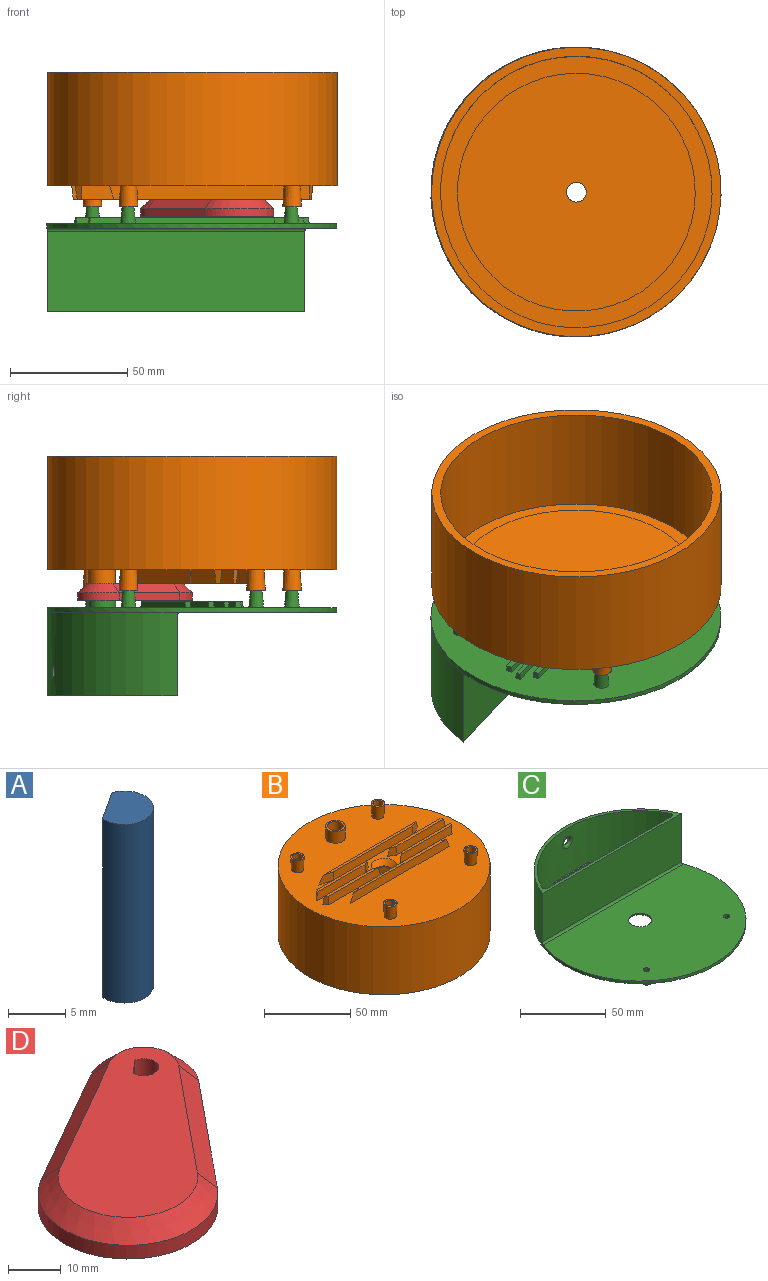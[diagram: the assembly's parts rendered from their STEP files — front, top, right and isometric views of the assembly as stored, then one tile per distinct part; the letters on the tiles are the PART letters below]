
ASSEMBLY  parts=4 mates=3
PART A: 4 faces, bbox 5.1x4.9x19.1 mm
  f0: plane 19.05x3.4mm, normal (-0.55,0.84,0), area 77.4mm2, adj f1,f2,f3
  f1: cylinder r=2.54mm len=19.05mm, axis (0,0,-1), area 214.3mm2, adj f0,f2,f3
  f2: plane 5.08x4.93mm, normal (0,0,1), area 17.4mm2, adj f0,f1
  f3: plane 5.08x4.93mm, normal (0,0,-1), area 17.4mm2, adj f0,f1
PART B: 61 faces, bbox 123.2x123.2x57.2 mm
  f0: plane 123.19x123.19mm, normal (0,0,1), area 10697.4mm2, adj f2,f6,f10,f14,f18,f22,f26,f31
  f1: cylinder r=57.79mm len=115.57mm, axis (0,0,1), area 16830.3mm2, adj f3,f8
  f2: cylinder r=61.59mm len=123.19mm, axis (0,0,1), area 18677.2mm2, adj f0,f3
  f3: plane 123.19x123.19mm, normal (0,0,-1), area 1428.9mm2, adj f1,f2
  f4: plane 101.22x101.22mm, normal (0,0,-1), area 7990.8mm2, adj f5,f7
  f5: cylinder r=4.22mm len=8.43mm, axis (0,0,-1), area 16.8mm2, adj f4,f6
  f6: cone r=7.39mm half-angle=45deg, axis (0,0,1), area 163.7mm2, adj f0,f5
  f7: cylinder r=50.61mm len=101.22mm, axis (0,0,-1), area 605.8mm2, adj f4,f8
  f8: plane 115.57x115.57mm, normal (0,0,-1), area 2443.5mm2, adj f1,f7
  f9: cone r=3.3mm half-angle=3deg, axis (0,0,-1), area 70.4mm2, adj f11,f12
  f10: cone r=3.49mm half-angle=3deg, axis (0,0,1), area 208.4mm2, adj f0,f11
  f11: plane 7.92x7.92mm, normal (0,0,1), area 24mm2, adj f9,f10
  f12: plane 6.07x6.07mm, normal (0,0,1), area 29mm2, adj f9
  f13: cone r=3.3mm half-angle=3deg, axis (0,0,-1), area 70.4mm2, adj f15,f16
  f14: cone r=3.49mm half-angle=3deg, axis (0,0,1), area 208.4mm2, adj f0,f15
  f15: plane 7.92x7.92mm, normal (0,0,1), area 24mm2, adj f13,f14
  f16: plane 6.07x6.07mm, normal (0,0,1), area 29mm2, adj f13
  f17: cone r=3.3mm half-angle=3deg, axis (0,0,-1), area 70.4mm2, adj f19,f20
  f18: cone r=3.49mm half-angle=3deg, axis (0,0,1), area 208.4mm2, adj f0,f19
  f19: plane 7.92x7.92mm, normal (0,0,1), area 24mm2, adj f17,f18
  f20: plane 6.07x6.07mm, normal (0,0,1), area 29mm2, adj f17
  f21: cone r=3.3mm half-angle=3deg, axis (0,0,-1), area 70.4mm2, adj f23,f24
  f22: cone r=3.49mm half-angle=3deg, axis (0,0,1), area 208.4mm2, adj f0,f23
  f23: plane 7.92x7.92mm, normal (0,0,1), area 24mm2, adj f21,f22
  f24: plane 6.07x6.07mm, normal (0,0,1), area 29mm2, adj f21
  f25: cylinder r=4.45mm len=8.89mm, axis (0,0,-1), area 230.6mm2, adj f27,f28
  f26: cylinder r=5.71mm len=11.43mm, axis (0,0,-1), area 296.4mm2, adj f0,f27
  f27: plane 11.43x11.43mm, normal (0,0,1), area 40.5mm2, adj f25,f26
  f28: plane 8.89x8.89mm, normal (0,0,1), area 40.8mm2, adj f25,f29
  f29: cylinder r=2.6mm len=5.21mm, axis (0,0,1), area 41.6mm2, adj f28,f30
  f30: plane 5.21x5.21mm, normal (0,0,1), area 21.3mm2, adj f29
  f31: plane 65.26x5.72mm, normal (0,-1,0.07), area 373.5mm2, adj f0,f32,f34,f35
  f32: plane 6.41x5.72mm, normal (0.37,-0.93,0.07), area 33mm2, adj f0,f31,f33,f35
  f33: plane 81.28x5.72mm, normal (0,1,0.07), area 450.8mm2, adj f0,f32,f34,f35
  f34: plane 9.73x5.72mm, normal (-0.25,-0.96,0.07), area 48.3mm2, adj f0,f31,f33,f35
  f35: plane 76.11x1.74mm, normal (0,0,1), area 122.9mm2, adj f31,f32,f33,f34
  f36: plane 65.26x5.72mm, normal (0,1,0.07), area 373.5mm2, adj f0,f37,f39,f40
  f37: plane 9.73x5.72mm, normal (-0.25,0.96,0.07), area 48.3mm2, adj f0,f36,f38,f40
  f38: plane 81.28x5.72mm, normal (0,-1,0.07), area 450.8mm2, adj f0,f37,f39,f40
  f39: plane 6.41x5.72mm, normal (0.37,0.93,0.07), area 33mm2, adj f0,f36,f38,f40
  f40: plane 76.11x1.74mm, normal (0,0,1), area 122.9mm2, adj f36,f37,f38,f39
  f41: plane 5.72x4.78mm, normal (0.48,-0.88,0.07), area 25.7mm2, adj f0,f42,f44,f45
  f42: plane 42.85x5.72mm, normal (0,1,0.07), area 240.4mm2, adj f0,f41,f43,f45
  f43: plane 5.72x2.54mm, normal (-0.78,0.62,0.07), area 15.7mm2, adj f0,f42,f44,f45
  f44: plane 40.21x5.72mm, normal (0,-1,0.07), area 227.7mm2, adj f0,f41,f43,f45
  f45: plane 42.48x1.74mm, normal (0,0,1), area 69.9mm2, adj f41,f42,f43,f44
  f46: plane 5.72x4.78mm, normal (0.48,0.88,0.07), area 25.7mm2, adj f0,f47,f49,f50
  f47: plane 40.21x5.72mm, normal (0,1,0.07), area 227.7mm2, adj f0,f46,f48,f50
  f48: plane 5.72x2.54mm, normal (-0.78,-0.62,0.07), area 15.7mm2, adj f0,f47,f49,f50
  f49: plane 42.85x5.72mm, normal (0,-1,0.07), area 240.4mm2, adj f0,f46,f48,f50
  f50: plane 42.48x1.74mm, normal (0,0,1), area 69.9mm2, adj f46,f47,f48,f49
  f51: plane 42.85x5.72mm, normal (0,1,0.07), area 240.4mm2, adj f0,f52,f54,f55
  f52: plane 5.72x4.78mm, normal (-0.48,-0.88,0.07), area 25.7mm2, adj f0,f51,f53,f55
  f53: plane 40.21x5.72mm, normal (0,-1,0.07), area 227.7mm2, adj f0,f52,f54,f55
  f54: plane 5.72x2.54mm, normal (0.78,0.62,0.07), area 15.7mm2, adj f0,f51,f53,f55
  f55: plane 42.48x1.74mm, normal (0,0,1), area 69.9mm2, adj f51,f52,f53,f54
  f56: plane 5.72x4.78mm, normal (-0.48,0.88,0.07), area 25.7mm2, adj f0,f57,f59,f60
  f57: plane 42.85x5.72mm, normal (0,-1,0.07), area 240.4mm2, adj f0,f56,f58,f60
  f58: plane 5.72x2.54mm, normal (0.78,-0.62,0.07), area 15.7mm2, adj f0,f57,f59,f60
  f59: plane 40.21x5.72mm, normal (0,1,0.07), area 227.7mm2, adj f0,f56,f58,f60
  f60: plane 42.48x1.74mm, normal (0,0,1), area 69.9mm2, adj f56,f57,f58,f59
PART C: 105 faces, bbox 123.4x126.4x44.7 mm
  f0: plane 8.89x8.89mm, normal (0,0,-1), area 42.4mm2, adj f27,f102
  f1: plane 123.44x123.44mm, normal (0,0,-1), area 10609.7mm2, adj f11,f25,f48,f49,f50,f51,f53,f54
  f2: plane 34.39x29.31mm, normal (0,0,1), area 638.9mm2, adj f19,f21,f22,f35,f99
  f3: plane 34.39x29.31mm, normal (0,0,1), area 638.9mm2, adj f5,f19,f20,f45,f100
  f4: plane 33.82x2.49mm, normal (0,0,1), area 56.4mm2, adj f19,f33
  f5: cylinder r=1.27mm len=33.75mm, axis (-1,0,0), area 67.3mm2, adj f3,f13,f20,f46
  f6: cylinder r=1.27mm len=25.4mm, axis (-1,0,0), area 50.7mm2, adj f13,f18,f39,f43
  f7: cylinder r=2.25mm len=4.5mm, axis (0,-1,0), area 0.3mm2, adj f8,f26
  f8: cylinder r=61.78mm len=114.3mm, axis (0,0,-1), area 5173.5mm2, adj f7,f10,f11,f16,f17,f24
  f9: cylinder r=59.88mm len=105.66mm, axis (0,0,-1), area 4385.5mm2, adj f14,f15,f17,f19,f26
  f10: plane 114.3x38.41mm, normal (0,0,1), area 9.8mm2, adj f8,f11
  f11: cylinder r=61.72mm len=123.44mm, axis (0,0,-1), area 739.5mm2, adj f1,f8,f10,f12,f23
  f12: plane 123.44x83.76mm, normal (0,0,1), area 8480.4mm2, adj f11,f23,f25,f92,f101
  f13: plane 102.3x34.29mm, normal (0,1,0), area 3460.2mm2, adj f5,f6,f14,f15,f17,f22,f34,f37
  f14: cylinder r=1.91mm len=34.29mm, axis (0,0,-1), area 134.6mm2, adj f9,f13,f17,f20
  f15: cylinder r=1.91mm len=34.29mm, axis (0,0,-1), area 134.6mm2, adj f9,f13,f17,f21
  f16: plane 114.3x34.29mm, normal (0,-1,0), area 3919.3mm2, adj f8,f17,f23
  f17: plane 114.3x38.31mm, normal (0,0,1), area 484.9mm2, adj f8,f9,f13,f14,f15,f16
  f18: plane 26.67x25.4mm, normal (0,0,1), area 616.5mm2, adj f6,f27,f40,f41,f42
  f19: torus R=58.61mm, axis (0,0,1), area 256.1mm2, adj f2,f3,f4,f9,f20,f21,f33,f35
  f20: torus R=0.64mm, axis (0,0,1), area 5.9mm2, adj f3,f5,f14,f19
  f21: torus R=0.64mm, axis (0,0,1), area 5.9mm2, adj f2,f15,f19,f22
  f22: cylinder r=1.27mm len=33.75mm, axis (-1,0,0), area 67.3mm2, adj f2,f13,f21,f36
  f23: cylinder r=1.27mm len=115.3mm, axis (1,0,0), area 228.8mm2, adj f11,f12,f16
  f24: cylinder r=2.25mm len=4.5mm, axis (0,-1,0), area 0.3mm2, adj f8,f26
  f25: torus R=8.65mm, axis (0,0,1), area 139.9mm2, adj f1,f12
  f26: bspline ~8.32x8.06mm, area 53.7mm2, adj f7,f9,f24
  f27: torus R=4.41mm, axis (0,0,1), area 60mm2, adj f0,f18
  f28: plane 28.83x4.45mm, normal (-1,0,0), area 128.1mm2, adj f33,f34,f45,f47
  f29: plane 27.94x4.45mm, normal (1,0,0), area 124.2mm2, adj f32,f34,f38,f40
  f30: plane 27.94x4.45mm, normal (-1,0,0), area 124.2mm2, adj f32,f34,f42,f44
  f31: plane 28.83x4.45mm, normal (1,0,0), area 128.1mm2, adj f33,f34,f35,f37
  f32: plane 29.21x4.45mm, normal (0,-1,0), area 129.8mm2, adj f29,f30,f34,f41
  f33: plane 34.54x6.35mm, normal (0,1,0), area 198.3mm2, adj f4,f19,f28,f31,f34,f35,f45
  f34: plane 34.8x30.73mm, normal (0,0,1), area 83.7mm2, adj f13,f28,f29,f30,f31,f32,f33,f37
  f35: cylinder r=1.91mm len=29.46mm, axis (0,1,0), area 87.5mm2, adj f2,f19,f31,f33,f36
  f36: bspline ~2.32x1.91mm, area 3.9mm2, adj f22,f35,f37
  f37: cylinder r=1.91mm len=5.08mm, axis (0,0,1), area 14.5mm2, adj f13,f31,f34,f36
  f38: cylinder r=1.91mm len=5.08mm, axis (0,0,1), area 14.5mm2, adj f13,f29,f34,f39
  f39: bspline ~2.32x1.91mm, area 3.9mm2, adj f6,f38,f40
  f40: cylinder r=1.91mm len=28.58mm, axis (0,1,0), area 82.7mm2, adj f18,f29,f39,f41
  f41: cylinder r=1.91mm len=29.21mm, axis (1,0,0), area 83.3mm2, adj f18,f32,f40,f42
  f42: cylinder r=1.91mm len=28.58mm, axis (0,-1,0), area 82.7mm2, adj f18,f30,f41,f43
  f43: bspline ~2.32x1.91mm, area 3.9mm2, adj f6,f42,f44
  f44: cylinder r=1.91mm len=5.08mm, axis (0,0,-1), area 14.5mm2, adj f13,f30,f34,f43
  f45: cylinder r=1.91mm len=29.46mm, axis (0,-1,0), area 87.5mm2, adj f3,f19,f28,f33,f46
  f46: bspline ~2.32x1.91mm, area 3.9mm2, adj f5,f45,f47
  f47: cylinder r=1.91mm len=5.08mm, axis (0,0,-1), area 14.5mm2, adj f13,f28,f34,f46
  f48: plane 66.04x2.54mm, normal (0,1,-0.07), area 167.7mm2, adj f1,f49,f51,f52
  f49: plane 2.54x2.54mm, normal (-1,0,-0.07), area 6mm2, adj f1,f48,f50,f52
  f50: plane 66.04x2.54mm, normal (0,-1,-0.07), area 167.7mm2, adj f1,f49,f51,f52
  f51: plane 2.54x2.54mm, normal (1,0,-0.07), area 6mm2, adj f1,f48,f50,f52
  f52: plane 65.68x2.18mm, normal (0,0,-1), area 143.5mm2, adj f48,f49,f50,f51
  f53: plane 66.04x2.54mm, normal (0,-1,-0.07), area 167.7mm2, adj f1,f54,f56,f57
  f54: plane 2.54x2.54mm, normal (1,0,-0.07), area 6mm2, adj f1,f53,f55,f57
  f55: plane 66.04x2.54mm, normal (0,1,-0.07), area 167.7mm2, adj f1,f54,f56,f57
  f56: plane 2.54x2.54mm, normal (-1,0,-0.07), area 6mm2, adj f1,f53,f55,f57
  f57: plane 65.68x2.18mm, normal (0,0,-1), area 143.5mm2, adj f53,f54,f55,f56
  f58: plane 39.29x2.54mm, normal (0,1,-0.07), area 99.8mm2, adj f1,f59,f62,f63
  f59: plane 2.54x2.19mm, normal (-1,0.03,-0.07), area 5.1mm2, adj f1,f58,f60,f63
  f60: plane 39.23x2.54mm, normal (0,-1,-0.07), area 99.6mm2, adj f1,f59,f61,f63
  f61: plane 2.87x2.54mm, normal (0.36,-0.93,-0.07), area 7.1mm2, adj f1,f60,f62,f63
  f62: plane 2.76x2.54mm, normal (0.37,0.93,-0.07), area 6.9mm2, adj f1,f58,f61,f63
  f63: plane 41.41x1.84mm, normal (0,0,-1), area 73.8mm2, adj f58,f59,f60,f61,f62
  f64: plane 2.76x2.54mm, normal (-0.37,0.93,-0.07), area 6.9mm2, adj f1,f65,f68,f69
  f65: plane 2.87x2.54mm, normal (-0.36,-0.93,-0.07), area 7.1mm2, adj f1,f64,f66,f69
  f66: plane 39.23x2.54mm, normal (0,-1,-0.07), area 99.6mm2, adj f1,f65,f67,f69
  f67: plane 2.54x2.19mm, normal (1,0.03,-0.07), area 5.1mm2, adj f1,f66,f68,f69
  f68: plane 39.29x2.54mm, normal (0,1,-0.07), area 99.8mm2, adj f1,f64,f67,f69
  f69: plane 41.41x1.84mm, normal (0,0,-1), area 73.8mm2, adj f64,f65,f66,f67,f68
  f70: plane 5.49x2.54mm, normal (0.42,-0.9,-0.07), area 14.2mm2, adj f1,f71,f73,f74
  f71: plane 40.95x2.54mm, normal (0,1,-0.07), area 103mm2, adj f1,f70,f72,f74
  f72: plane 2.54x2.54mm, normal (-1,0,-0.07), area 6mm2, adj f1,f71,f73,f74
  f73: plane 35.5x2.54mm, normal (0,-1,-0.07), area 90.1mm2, adj f1,f70,f72,f74
  f74: plane 39.97x2.18mm, normal (0,0,-1), area 82.2mm2, adj f70,f71,f72,f73
  f75: plane 2.54x2.54mm, normal (1,0,-0.07), area 6mm2, adj f1,f76,f78,f79
  f76: plane 40.95x2.54mm, normal (0,1,-0.07), area 103mm2, adj f1,f75,f77,f79
  f77: plane 5.49x2.54mm, normal (-0.42,-0.9,-0.07), area 14.2mm2, adj f1,f76,f78,f79
  f78: plane 35.5x2.54mm, normal (0,-1,-0.07), area 90.1mm2, adj f1,f75,f77,f79
  f79: plane 39.97x2.18mm, normal (0,0,-1), area 82.2mm2, adj f75,f76,f77,f78
  f80: plane 39.38x2.54mm, normal (0,-1,-0.07), area 99mm2, adj f1,f81,f83,f84
  f81: plane 5.44x2.54mm, normal (0.42,0.9,-0.07), area 14.1mm2, adj f1,f80,f82,f84
  f82: plane 33.97x2.54mm, normal (0,1,-0.07), area 86.2mm2, adj f1,f81,f83,f84
  f83: plane 2.54x2.54mm, normal (-1,0,-0.07), area 6mm2, adj f1,f80,f82,f84
  f84: plane 38.4x2.18mm, normal (0,0,-1), area 78.8mm2, adj f80,f81,f82,f83
  f85: plane 33.97x2.54mm, normal (0,1,-0.07), area 86.2mm2, adj f1,f86,f88,f89
  f86: plane 5.44x2.54mm, normal (-0.42,0.9,-0.07), area 14.1mm2, adj f1,f85,f87,f89
  f87: plane 39.38x2.54mm, normal (0,-1,-0.07), area 99mm2, adj f1,f86,f88,f89
  f88: plane 2.54x2.54mm, normal (1,0,-0.07), area 6mm2, adj f1,f85,f87,f89
  f89: plane 38.4x2.18mm, normal (0,0,-1), area 78.8mm2, adj f85,f86,f87,f88
  f90: cone r=3.17mm half-angle=5deg, axis (0,0,1), area 130.8mm2, adj f1,f91
  f91: cone r=1.91mm half-angle=5deg, axis (0,0,-1), area 101.7mm2, adj f90,f92
  f92: cylinder r=1.91mm len=3.81mm, axis (0,0,-1), area 22.8mm2, adj f12,f91
  f93: cone r=3.17mm half-angle=5deg, axis (0,0,1), area 130.8mm2, adj f1,f94
  f94: cone r=1.91mm half-angle=5deg, axis (0,0,-1), area 101.7mm2, adj f93,f99
  f95: cone r=3.17mm half-angle=5deg, axis (0,0,1), area 130.8mm2, adj f1,f96
  f96: cone r=1.91mm half-angle=5deg, axis (0,0,-1), area 101.7mm2, adj f95,f100
  f97: cone r=3.17mm half-angle=5deg, axis (0,0,1), area 130.8mm2, adj f1,f98
  f98: cone r=1.91mm half-angle=5deg, axis (0,0,-1), area 101.7mm2, adj f97,f101
  f99: cylinder r=1.91mm len=3.81mm, axis (0,0,-1), area 22.8mm2, adj f2,f94
  f100: cylinder r=1.91mm len=3.81mm, axis (0,0,-1), area 22.8mm2, adj f3,f96
  f101: cylinder r=1.91mm len=3.81mm, axis (0,0,-1), area 22.8mm2, adj f12,f98
  f102: cylinder r=4.45mm len=8.89mm, axis (0,0,1), area 177.3mm2, adj f0,f104
  f103: cylinder r=5.71mm len=11.43mm, axis (0,0,1), area 228mm2, adj f1,f104
  f104: plane 11.43x11.43mm, normal (0,0,-1), area 40.5mm2, adj f102,f103
PART D: 16 faces, bbox 55x50.8x7 mm
  f0: plane 7.62x7.62mm, normal (0,0,-1), area 23.5mm2, adj f11,f14,f15
  f1: cylinder r=17.02mm len=31.78mm, axis (0,0,-1), area 189.5mm2, adj f2,f4,f6,f10
  f2: plane 27.54x22.5mm, normal (0.77,-0.63,0), area 112.9mm2, adj f1,f3,f6,f9
  f3: cylinder r=10.45mm len=17.05mm, axis (0,0,-1), area 92.1mm2, adj f2,f4,f6,f7
  f4: plane 30.85x17.68mm, normal (-0.5,0.87,0), area 112.9mm2, adj f1,f3,f6,f8
  f5: plane 47.43x43.23mm, normal (0,0,1), area 1050.6mm2, adj f7,f8,f9,f10,f14,f15
  f6: plane 55.05x50.85mm, normal (0,0,-1), area 1509.2mm2, adj f1,f2,f3,f4,f12
  f7: cone r=6.64mm half-angle=45deg, axis (0,0,-1), area 127.7mm2, adj f3,f5,f8,f9
  f8: plane 32.75x20.99mm, normal (-0.35,0.61,0.71), area 191.6mm2, adj f4,f5,f7,f10
  f9: plane 29.95x25.45mm, normal (0.55,-0.45,0.71), area 191.6mm2, adj f2,f5,f7,f10
  f10: cone r=13.21mm half-angle=45deg, axis (0,0,-1), area 285.6mm2, adj f1,f5,f8,f9
  f11: cylinder r=3.81mm len=7.62mm, axis (0,0,-1), area 121.6mm2, adj f0,f13
  f12: cylinder r=6.35mm len=12.7mm, axis (0,0,-1), area 202.7mm2, adj f6,f13
  f13: plane 12.7x12.7mm, normal (0,0,-1), area 81.1mm2, adj f11,f12
  f14: plane 6.99x3.13mm, normal (0.68,-0.73,0), area 29.9mm2, adj f0,f5,f15
  f15: cylinder r=2.82mm len=6.99mm, axis (0,0,-1), area 89.8mm2, adj f0,f5,f14
PLACE A rot(axis=(0,0,1),113.3deg) t=(-247.96,97.75,-32.9)mm
PLACE B rot(axis=(-0.14,0.99,0),180deg) t=(-272.97,43.89,-27.86)mm
PLACE C rot(axis=(-0.14,0.99,0),180deg) t=(-273.18,44,-47.82)mm
PLACE D rot(axis=(0,0,1),103.5deg) t=(-245.63,91.53,-44.65)mm
MATE fastened B.f21 <-> C.f93  axis (0,0,-1) through (-315.46,71.02,-40.56)mm
MATE revolute D.f11 <-> C.f27  axis (0,0,-1) through (-284.5,82.18,-44.65)mm
MATE fastened D.f14 <-> A.f0  axis (0.55,0.83,0) through (-285.52,80.65,-41.15)mm
